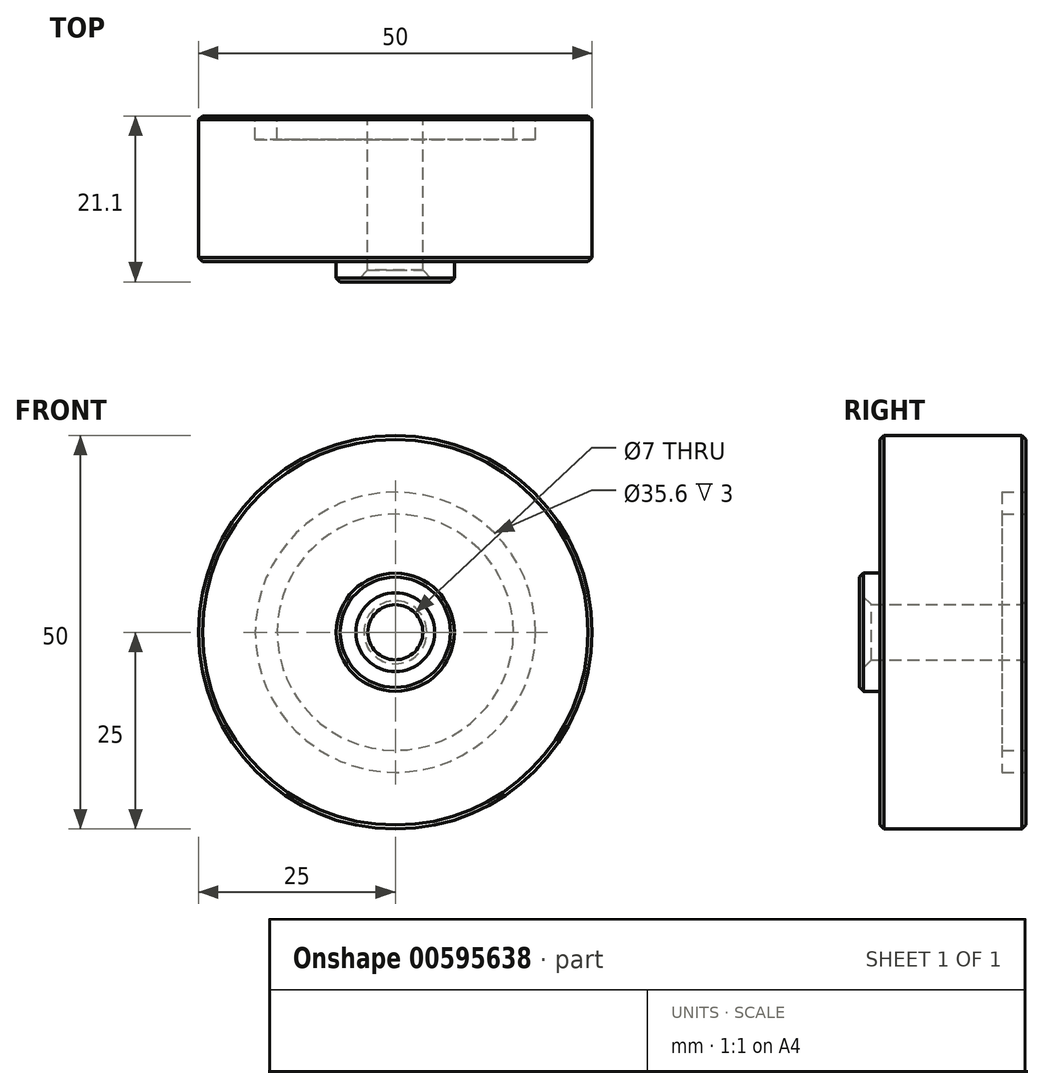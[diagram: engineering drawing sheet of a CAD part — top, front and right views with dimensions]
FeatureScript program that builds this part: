
annotation { "Feature Type Name" : "Feature", "Feature Type Description" : "" }
export const myFeature = defineFeature(function(context is Context, id is Id, definition is map)
    precondition{}
    {
        {
            var Q0;
            Q0=qCreatedBy(makeId("Front.planeOp"),FACE);
            var sketch = newSketch(context, id + "F0", { "sketchPlane" : qUnion([Q0])});
            skCircle(sketch, "E0", {"center": v(0, 0) * mm, "radius": 25 * mm});
            skCircle(sketch, "E1", {"center": v(0, 0) * mm, "radius": 3.5 * mm});
            skSolve(sketch);
        }
        {
            var Q0;
            Q0 = qSketchRegion(id + "F0", true);
            extrude(context, id + "F1", {"entities" : qUnion([Q0]), "depth" : 18.5 * mm, "offsetDistance" : 25 * mm});
        }
        {
            var Q0;
            Q0=makeQuery(id+"F1.opExtrude","CAP_FACE",FACE,{"disambiguationData":[OSD([sQuery(id+"F0.wireOp",EDGE,"E0"),sQuery(id+"F0.wireOp",EDGE,"E1")])],"isStart":false});
            var sketch = newSketch(context, id + "F2", { "sketchPlane" : qUnion([Q0])});
            skCircle(sketch, "E2", {"center": v(0, 0) * mm, "radius": 7.5 * mm});
            skCircle(sketch, "E3", {"center": v(0, 0) * mm, "radius": 3.5 * mm});
            skSolve(sketch);
        }
        {
            var Q0;
            Q0 = qSketchRegion(id + "F2", true);
            extrude(context, id + "F3", {"entities" : qUnion([Q0]), "operationType" : NewBodyOperationType.ADD, "depth" : 2.6 * mm, "offsetDistance" : 25 * mm});
        }
        {
            var Q0;
            Q0=makeQuery(id+"F1.opExtrude","CAP_FACE",FACE,{"disambiguationData":[OSD([sQuery(id+"F0.wireOp",EDGE,"E0"),sQuery(id+"F0.wireOp",EDGE,"E1")])],"isStart":true});
            var sketch = newSketch(context, id + "F4", { "sketchPlane" : qUnion([Q0])});
            skCircle(sketch, "E4", {"center": v(0, 0) * mm, "radius": 15 * mm});
            skCircle(sketch, "E5", {"center": v(0, 0) * mm, "radius": 17.8 * mm});
            skSolve(sketch);
        }
        {
            var Q0;
            Q0 = qSketchRegion(id + "F4", true);
            extrude(context, id + "F5", {"entities" : qUnion([Q0]), "operationType" : NewBodyOperationType.REMOVE, "oppositeDirection" : true, "depth" : 3 * mm, "offsetDistance" : 25 * mm});
        }
        {
            var Q0;
            Q0=makeQuery(id+"F1.opExtrude","CAP_EDGE",EDGE,{"disambiguationData":[OSD([sQuery(id+"F0.wireOp",EDGE,"E0")])],"isStart":true});
            var Q1;
            Q1=makeQuery(id+"F1.opExtrude","CAP_EDGE",EDGE,{"disambiguationData":[OSD([sQuery(id+"F0.wireOp",EDGE,"E0")])],"isStart":false});
            var Q2;
            Q2=makeQuery(id+"F1.opExtrude","CAP_EDGE",EDGE,{"disambiguationData":[OSD([sQuery(id+"F0.wireOp",EDGE,"E1")])],"isStart":true});
            var Q3;
            Q3=makeQuery(id+"F3.opExtrude","CAP_EDGE",EDGE,{"disambiguationData":[OSD([sQuery(id+"F2.wireOp",EDGE,"E2")])],"isStart":false});
            chamfer(context, id + "F6", {"entities" : qUnion([Q0, Q1, Q2, Q3]), "chamferType" : ChamferType.OFFSET_ANGLE, "width" : .5 * mm, "oppositeDirection" : false, "angle" : 45 * degree, "tangentPropagation" : true});
        }
        {
            var Q0;
            Q0=makeQuery(id+"F3.opExtrude","CAP_EDGE",EDGE,{"disambiguationData":[OSD([sQuery(id+"F2.wireOp",EDGE,"E3")])],"isStart":false});
            chamfer(context, id + "F7", {"entities" : qUnion([Q0]), "width" : 1.5 * mm, "tangentPropagation" : true});
        }
    });
